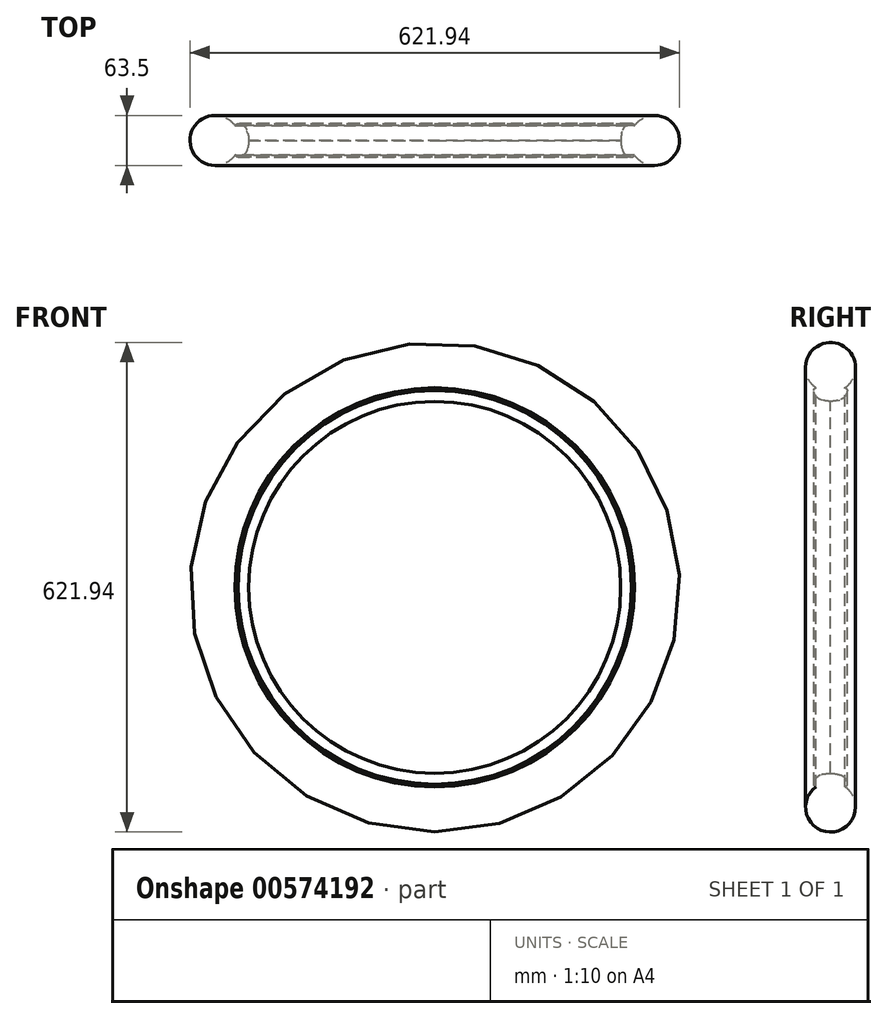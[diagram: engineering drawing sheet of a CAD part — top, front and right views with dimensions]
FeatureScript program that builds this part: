
annotation { "Feature Type Name" : "Feature", "Feature Type Description" : "" }
export const myFeature = defineFeature(function(context is Context, id is Id, definition is map)
    precondition{}
    {
        {
            var Q0;
            Q0=qCreatedBy(makeId("Right.planeOp"),FACE);
            var sketch = newSketch(context, id + "F0", { "sketchPlane" : qUnion([Q0])});
            skLineSegment(sketch, "E0", {"start": v(45.79, 237.5) * mm, "end": v(43.18, 238.2) * mm});
            skLineSegment(sketch, "E1", {"start": v(33.75, 249.88) * mm, "end": v(33.75, 250.47) * mm});
            skLineSegment(sketch, "E2", {"start": v(32.52, 252.25) * mm, "end": v(33.75, 252.65) * mm});
            skPoint(sketch, "E3.visualSharp", {"position": v(33.75, 252.65) * mm});
            skArc(sketch, "E3.filletArc", {"start": v(36.39, 253.5) * mm, "mid": v(34.48, 252.12) * mm, "end": v(33.75, 249.88) * mm});
            skPoint(sketch, "E4.visualSharp", {"position": v(33.75, 240.7) * mm});
            skArc(sketch, "E4.filletArc", {"start": v(33.75, 250.47) * mm, "mid": v(36.38, 242.73) * mm, "end": v(43.18, 238.2) * mm});
            skPoint(sketch, "E5.visualSharp", {"position": v(55.6, 234.89) * mm});
            skArc(sketch, "E5.filletArc", {"start": v(45.79, 237.5) * mm, "mid": v(50.35, 236.58) * mm, "end": v(55, 236.22) * mm});
            skLineSegment(sketch, "E6", {"start": v(55, -233.23) * mm, "end": v(55, 310.97) * mm, "construction": true});
            skArc(sketch, "E7.MirrorCS", {"start": v(64.21, 237.5) * mm, "mid": v(59.65, 236.58) * mm, "end": v(55, 236.22) * mm});
            skLineSegment(sketch, "E8.MirrorCS", {"start": v(64.21, 237.5) * mm, "end": v(66.82, 238.2) * mm});
            skArc(sketch, "E9.MirrorCS", {"start": v(76.25, 250.47) * mm, "mid": v(73.62, 242.73) * mm, "end": v(66.82, 238.2) * mm});
            skLineSegment(sketch, "E10.MirrorCS", {"start": v(76.25, 249.88) * mm, "end": v(76.25, 250.47) * mm});
            skArc(sketch, "E11.MirrorCS", {"start": v(73.61, 253.5) * mm, "mid": v(75.52, 252.12) * mm, "end": v(76.25, 249.88) * mm});
            skCircle(sketch, "E12", {"center": v(55, 279.22) * mm, "radius": 31.75 * mm});
            skPoint(sketch, "E12.third.point", {"position": v(55, 310.97) * mm});
            skLineSegment(sketch, "E13", {"start": v(-53.01, 0) * mm, "end": v(55, 0) * mm, "construction": true});
            skSolve(sketch);
        }
        {
            var Q0;
            Q0=makeQuery(id+"F0.imprint","IMPRINT",FACE,{"disambiguationData":[TD([[makeQuery(id+"F0.imprint","IMPRINT",EDGE,{"derivedFrom":sQuery(id+"F0.wireOp",EDGE,"E0")}),-1.0]])]});
            var Q1;
            {var subQ0=sQuery(id+"F0.wireOp",EDGE,"E12");var subQ1=makeQuery(id+"F0.imprint","INTERSECT",VERTEX,{"derivedFrom":[sQuery(id+"F0.wireOp",EDGE,"E3.filletArc"),subQ0]});Q1=makeQuery(id+"F0.imprint","IMPRINT",FACE,{"disambiguationData":[TD([[makeQuery(id+"F0.imprint","IMPRINT",EDGE,{"disambiguationData":[TD([[subQ1,-1.0]])],"derivedFrom":subQ0}),1.0]])]});}
            var Q2;
            Q2=sQuery(id+"F0.wireOp",EDGE,"E13");
            revolve(context, id + "F1", {"entities" : qUnion([Q0, Q1]), "axis" : qUnion([Q2]), "revolveType" : RevolveType.FULL});
        }
    });
